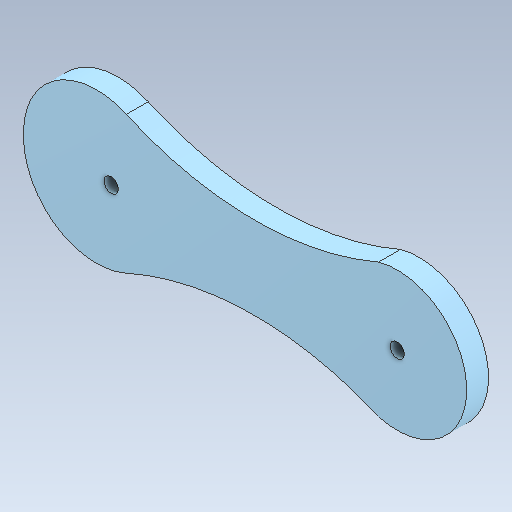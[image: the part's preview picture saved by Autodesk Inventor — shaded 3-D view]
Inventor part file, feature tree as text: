
AUTODESK INVENTOR PART (.ipt)
format: ipt  version: 2020.3 (Build 243373000, 373)  size: 172,544 bytes
history: native  units: in
note: dims shown in document units (in); Inventor stores cm internally (conversion verified against a paired STEP export)
features: other x4, sketch x1, direct_edit x1, fillet x1
ambient origin geometry x8: Origin, YZ Plane, XZ Plane, XY Plane, X Axis, Y Axis, Z Axis, Center Point
bodies: Solid1 (feature_tree)
feature tree (7):
  other  "Part 18.ipt"
  sketch  "Sketch1"  dims[d1=0.1969in d2=0.7874in]
  direct_edit  "Direct Edit1"
  fillet  "Fillet1"  Radius=0.7874in
  other  "Solid1::Part 18.ipt"
  other  "TaggingFeature1"
  other  "Size1"
